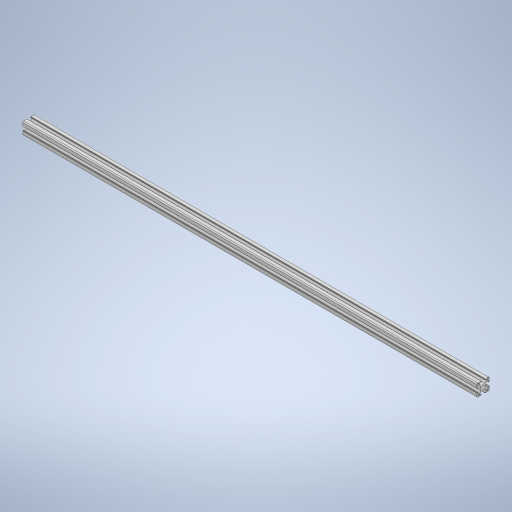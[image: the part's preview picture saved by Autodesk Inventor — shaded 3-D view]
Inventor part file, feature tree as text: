
AUTODESK INVENTOR PART (.ipt)
format: ipt  version: 2023 (Build 270158000, 158)  size: 374,784 bytes
history: native  units: mm
features: extrude x1, mirror x1, pattern_circular x1, sketch x1
ambient origin geometry x8: Origin, YZ Plane, XZ Plane, XY Plane, X Axis, Y Axis, Z Axis, Center Point
bodies: Solid1 (feature_tree)
feature tree (4):
  extrude  "Extrusion1"  TaperAngle=45.0deg  [1 undecoded]
  mirror  "Mirror1"
  pattern_circular  "Circular Pattern1"  Angle=45.0deg  [1 undecoded]
  sketch  "Sketch1"  dims[d0=3.4mm d1=45.0deg d3=45.0deg d4=2.5mm d5=135.0deg d6=1.0mm d7=4.1mm d8=5.2mm d9=8.25mm d10=15.0mm d11=2.2mm d12=5.8mm d13=1.5mm d14=1.5mm d15=1.0mm d16=1.0mm d17=1.0mm d18=1100.0mm d19=0.0mm d20=40.0mm d21=360.0deg]
note: 2 required parameter values undecoded (feature->parameter linkage not recoverable at this tier; creation-order binding heuristic only, values carry confidence <= 0.55)
